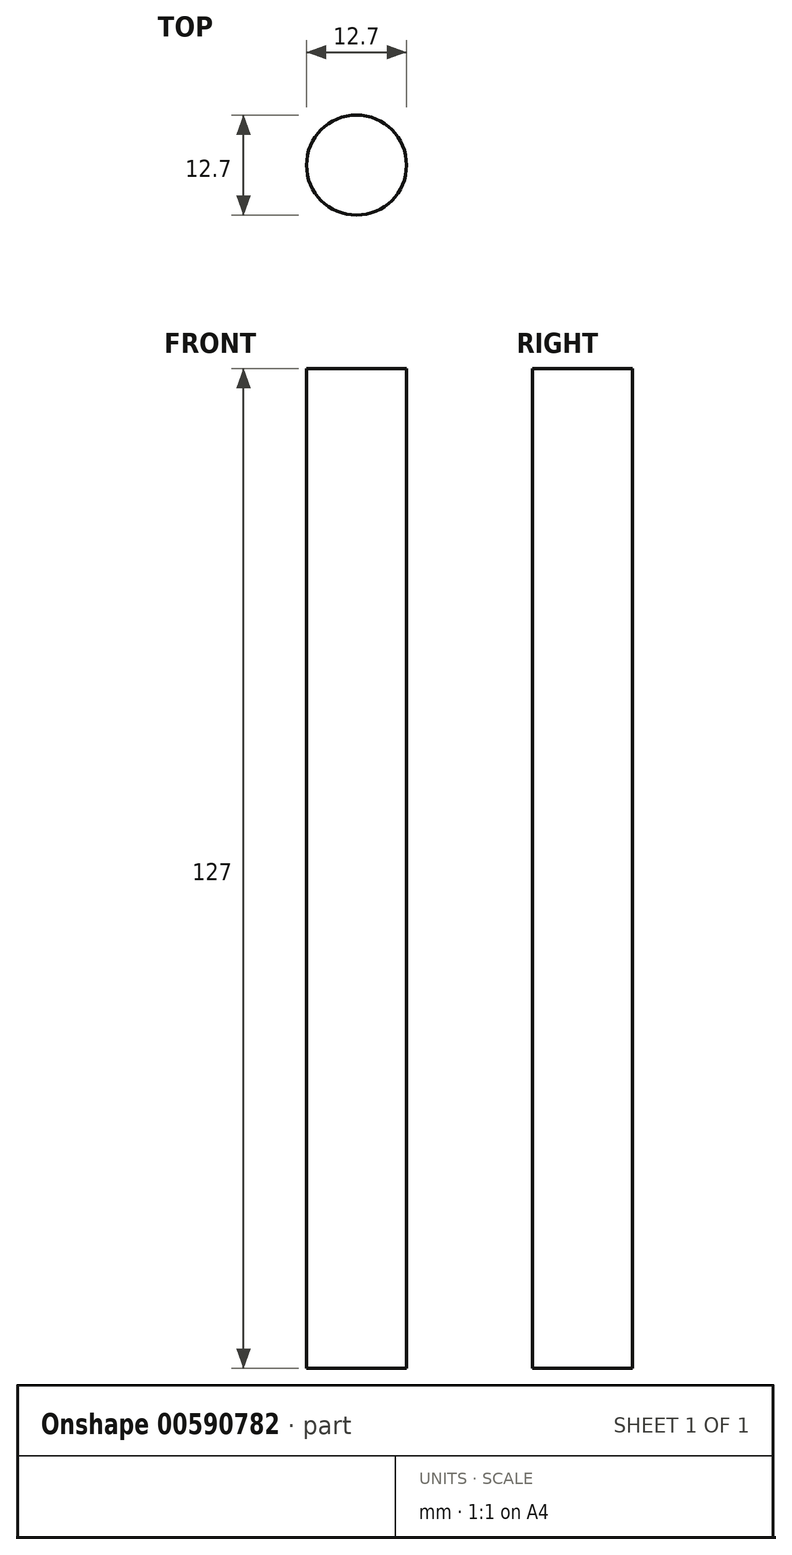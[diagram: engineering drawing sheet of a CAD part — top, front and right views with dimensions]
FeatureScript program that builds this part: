
annotation { "Feature Type Name" : "Feature", "Feature Type Description" : "" }
export const myFeature = defineFeature(function(context is Context, id is Id, definition is map)
    precondition{}
    {
        {
            var Q0;
            Q0=qCreatedBy(makeId("Top.planeOp"),FACE);
            var sketch = newSketch(context, id + "F0", { "sketchPlane" : qUnion([Q0])});
            skCircle(sketch, "E0", {"center": v(0, 0) * mm, "radius": 6.35 * mm});
            skSolve(sketch);
        }
        {
            var Q0;
            Q0 = qSketchRegion(id + "F0", true);
            extrude(context, id + "F1", {"entities" : qUnion([Q0]), "depth" : 127 * mm, "offsetDistance" : 25.4 * mm});
        }
    });
